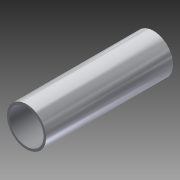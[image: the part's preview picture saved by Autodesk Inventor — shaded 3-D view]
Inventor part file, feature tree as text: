
AUTODESK INVENTOR PART (.ipt)
format: ipt  version: 2015 (Build 190159000, 159)  size: 88,576 bytes
history: native  units: in
note: dims shown in document units (in); Inventor stores cm internally (conversion verified against a paired STEP export)
features: extrude x1, sketch x1
ambient origin geometry x8: Origin, YZ Plane, XZ Plane, XY Plane, X Axis, Y Axis, Z Axis, Center Point
bodies: Solid1 (feature_tree)
feature tree (2):
  extrude  "Extrusion1"  Depth=1.625in
  sketch  "Sketch1"  dims[d0=0.5in d1=0.03in d2=1.625in d3=0.0in]
